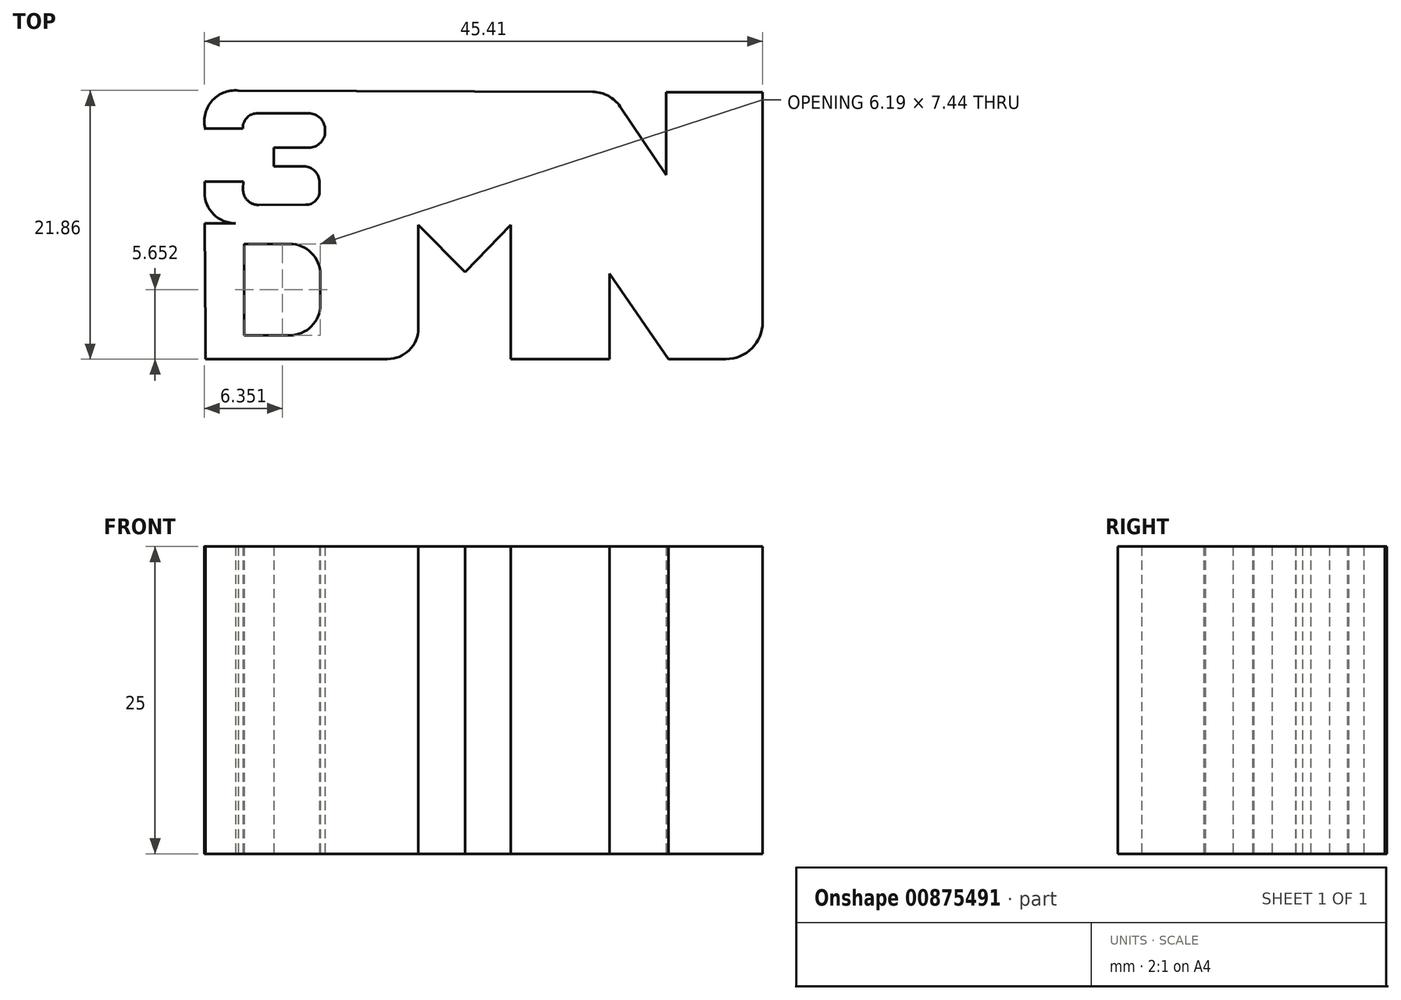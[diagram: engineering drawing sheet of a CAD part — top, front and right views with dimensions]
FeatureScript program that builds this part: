
annotation { "Feature Type Name" : "Feature", "Feature Type Description" : "" }
export const myFeature = defineFeature(function(context is Context, id is Id, definition is map)
    precondition{}
    {
        {
            var Q0;
            Q0=qCreatedBy(makeId("Top.planeOp"),FACE);
            var sketch = newSketch(context, id + "F0", { "sketchPlane" : qUnion([Q0])});
            skLineSegment(sketch, "E0.top", {"start": v(-7.98, -11.54) * mm, "end": v(-22.79, -11.54) * mm});
            skLineSegment(sketch, "E0.left", {"start": v(22.52, 10.16) * mm, "end": v(22.52, -8.54) * mm});
            skPoint(sketch, "E1.visualSharp", {"position": v(-22.79, 10.2) * mm});
            skArc(sketch, "E1.filletArc", {"start": v(-20.14, 10.3) * mm, "mid": v(-22.31, 9.42) * mm, "end": v(-22.79, 7.11) * mm});
            skPoint(sketch, "E2.visualSharp", {"position": v(22.52, -11.54) * mm});
            skArc(sketch, "E2.filletArc", {"start": v(19.52, -11.54) * mm, "mid": v(21.65, -10.66) * mm, "end": v(22.52, -8.54) * mm});
            skLineSegment(sketch, "E3.left", {"start": v(-5.48, -0.6) * mm, "end": v(-5.48, -9.04) * mm});
            skLineSegment(sketch, "E3.right", {"start": v(2.04, -0.6) * mm, "end": v(2.04, -11.54) * mm});
            skLineSegment(sketch, "E4", {"start": v(-5.48, -0.6) * mm, "end": v(-1.67, -4.45) * mm});
            skLineSegment(sketch, "E5", {"start": v(-1.67, -4.45) * mm, "end": v(2.04, -0.6) * mm});
            skArc(sketch, "E6.filletArc", {"start": v(-7.98, -11.54) * mm, "mid": v(-6.22, -10.8) * mm, "end": v(-5.48, -9.04) * mm});
            skLineSegment(sketch, "E7", {"start": v(10.08, -4.58) * mm, "end": v(10.08, -11.54) * mm});
            skLineSegment(sketch, "E8", {"start": v(10.08, -4.58) * mm, "end": v(14.86, -11.54) * mm});
            skLineSegment(sketch, "E9", {"start": v(2.04, -11.54) * mm, "end": v(10.08, -11.54) * mm});
            skLineSegment(sketch, "E10", {"start": v(14.86, -11.54) * mm, "end": v(19.52, -11.54) * mm});
            skLineSegment(sketch, "E11", {"start": v(14.69, 10.16) * mm, "end": v(14.69, 3.46) * mm});
            skLineSegment(sketch, "E12", {"start": v(14.69, 3.46) * mm, "end": v(10.93, 9) * mm});
            skLineSegment(sketch, "E13", {"start": v(-20.14, 10.3) * mm, "end": v(8.7, 10.2) * mm});
            skLineSegment(sketch, "E14", {"start": v(14.69, 10.16) * mm, "end": v(22.52, 10.16) * mm});
            skPoint(sketch, "E15.visualSharp", {"position": v(10.13, 10.19) * mm});
            skArc(sketch, "E15.filletArc", {"start": v(10.93, 9) * mm, "mid": v(9.97, 9.88) * mm, "end": v(8.7, 10.2) * mm});
            skLineSegment(sketch, "E16.bottom", {"start": v(-19.63, -2.17) * mm, "end": v(-15.94, -2.17) * mm});
            skLineSegment(sketch, "E16.top", {"start": v(-19.63, -9.6) * mm, "end": v(-15.94, -9.6) * mm});
            skLineSegment(sketch, "E16.right", {"start": v(-13.44, -4.67) * mm, "end": v(-13.44, -7.1) * mm});
            skPoint(sketch, "E17.visualSharp", {"position": v(-13.44, -2.17) * mm});
            skArc(sketch, "E17.filletArc", {"start": v(-13.44, -4.67) * mm, "mid": v(-14.18, -2.9) * mm, "end": v(-15.94, -2.17) * mm});
            skPoint(sketch, "E18.visualSharp", {"position": v(-13.44, -9.6) * mm});
            skArc(sketch, "E18.filletArc", {"start": v(-15.94, -9.6) * mm, "mid": v(-14.18, -8.87) * mm, "end": v(-13.44, -7.1) * mm});
            skLineSegment(sketch, "E19", {"start": v(-22.79, -9.6) * mm, "end": v(-22.79, -11.54) * mm});
            skLineSegment(sketch, "E20", {"start": v(-19.63, -2.17) * mm, "end": v(-19.63, -9.6) * mm});
            skLineSegment(sketch, "E21", {"start": v(-22.86, -0.5) * mm, "end": v(-22.79, -9.6) * mm});
            skLineSegment(sketch, "E22", {"start": v(-22.79, 7.22) * mm, "end": v(-19.75, 7.22) * mm});
            skLineSegment(sketch, "E23", {"start": v(-19.75, 7.22) * mm, "end": v(-19.75, 7.27) * mm});
            skLineSegment(sketch, "E24", {"start": v(-18.55, 8.47) * mm, "end": v(-14.43, 8.47) * mm});
            skLineSegment(sketch, "E25", {"start": v(-13.06, 7.1) * mm, "end": v(-13.06, 6.98) * mm});
            skLineSegment(sketch, "E26", {"start": v(-14.38, 5.67) * mm, "end": v(-17.25, 5.67) * mm});
            skLineSegment(sketch, "E27", {"start": v(-17.25, 5.67) * mm, "end": v(-17.25, 4.13) * mm});
            skLineSegment(sketch, "E28", {"start": v(-17.25, 4.13) * mm, "end": v(-14.8, 4.13) * mm});
            skLineSegment(sketch, "E29", {"start": v(-13.5, 2.84) * mm, "end": v(-13.5, 2.15) * mm});
            skLineSegment(sketch, "E30", {"start": v(-14.63, 1.02) * mm, "end": v(-18.47, 1) * mm});
            skLineSegment(sketch, "E31", {"start": v(-19.74, 2.32) * mm, "end": v(-19.71, 2.89) * mm});
            skLineSegment(sketch, "E32", {"start": v(-19.71, 2.89) * mm, "end": v(-22.86, 2.92) * mm});
            skLineSegment(sketch, "E33", {"start": v(-22.79, 7.22) * mm, "end": v(-22.79, 7.11) * mm});
            skLineSegment(sketch, "E34", {"start": v(-22.86, 2.92) * mm, "end": v(-22.86, 2) * mm});
            skPoint(sketch, "E35.visualSharp", {"position": v(-19.8, 1) * mm});
            skArc(sketch, "E35.filletArc", {"start": v(-19.74, 2.32) * mm, "mid": v(-19.4, 1.4) * mm, "end": v(-18.47, 1) * mm});
            skPoint(sketch, "E36.visualSharp", {"position": v(-13.5, 1.02) * mm});
            skArc(sketch, "E36.filletArc", {"start": v(-14.63, 1.02) * mm, "mid": v(-13.83, 1.35) * mm, "end": v(-13.5, 2.15) * mm});
            skPoint(sketch, "E37.visualSharp", {"position": v(-13.51, 4.13) * mm});
            skArc(sketch, "E37.filletArc", {"start": v(-13.5, 2.84) * mm, "mid": v(-13.9, 3.76) * mm, "end": v(-14.8, 4.13) * mm});
            skPoint(sketch, "E38.visualSharp", {"position": v(-13.06, 5.67) * mm});
            skArc(sketch, "E38.filletArc", {"start": v(-14.38, 5.67) * mm, "mid": v(-13.45, 6.05) * mm, "end": v(-13.06, 6.98) * mm});
            skPoint(sketch, "E39.visualSharp", {"position": v(-13.06, 8.47) * mm});
            skArc(sketch, "E39.filletArc", {"start": v(-13.06, 7.1) * mm, "mid": v(-13.46, 8.07) * mm, "end": v(-14.43, 8.47) * mm});
            skPoint(sketch, "E40.visualSharp", {"position": v(-19.75, 8.47) * mm});
            skArc(sketch, "E40.filletArc", {"start": v(-18.55, 8.47) * mm, "mid": v(-19.4, 8.11) * mm, "end": v(-19.75, 7.27) * mm});
            skPoint(sketch, "E41.visualSharp", {"position": v(-22.86, -0.5) * mm});
            skArc(sketch, "E41.filletArc", {"start": v(-22.86, 2) * mm, "mid": v(-22.13, 0.24) * mm, "end": v(-20.36, -0.5) * mm});
            skLineSegment(sketch, "E42", {"start": v(-22.86, -0.5) * mm, "end": v(-20.36, -0.5) * mm});
            skSolve(sketch);
        }
        {
            var Q0;
            Q0=makeQuery(id+"F0.imprint","IMPRINT",FACE,{"disambiguationData":[TD([[makeQuery(id+"F0.imprint","IMPRINT",EDGE,{"derivedFrom":sQuery(id+"F0.wireOp",EDGE,"E0.top")}),-1.0]])]});
            extrude(context, id + "F1", {"entities" : qUnion([Q0]), "depth" : 25 * mm, "offsetDistance" : 25 * mm});
        }
    });
